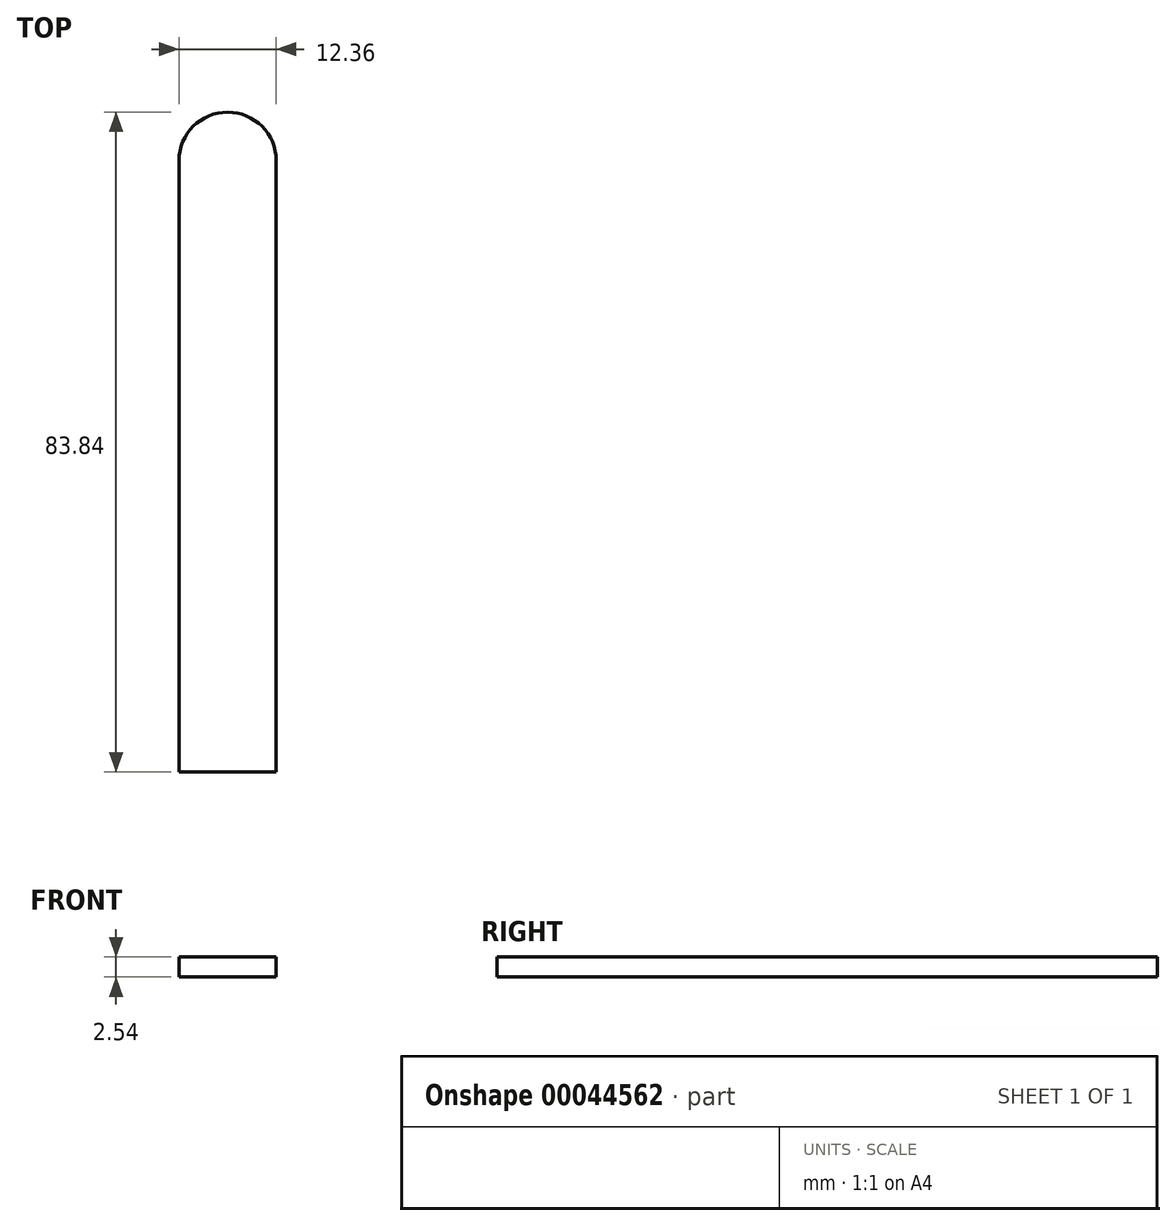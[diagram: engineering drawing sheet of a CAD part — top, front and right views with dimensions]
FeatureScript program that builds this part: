
annotation { "Feature Type Name" : "Feature", "Feature Type Description" : "" }
export const myFeature = defineFeature(function(context is Context, id is Id, definition is map)
    precondition{}
    {
        {
            var Q0;
            Q0=qCreatedBy(makeId("Top.planeOp"),FACE);
            var sketch = newSketch(context, id + "F0", { "sketchPlane" : qUnion([Q0])});
            skLineSegment(sketch, "E0.rect.bottom", {"start": v(6.18, 38.83) * mm, "end": v(-6.18, 38.83) * mm});
            skLineSegment(sketch, "E0.rect.top", {"start": v(6.18, -38.83) * mm, "end": v(-6.18, -38.83) * mm});
            skLineSegment(sketch, "E0.rect.left", {"start": v(6.18, 38.83) * mm, "end": v(6.18, -38.83) * mm});
            skLineSegment(sketch, "E0.rect.right", {"start": v(-6.18, 38.83) * mm, "end": v(-6.18, -38.83) * mm});
            skPoint(sketch, "E0.rect.middle", {"position": v(0, 0) * mm});
            skArc(sketch, "E1", {"start": v(-6.18, 38.83) * mm, "mid": v(0, 45) * mm, "end": v(6.18, 38.83) * mm});
            skSolve(sketch);
        }
        {
            var Q0;
            Q0 = qSketchRegion(id + "F0", true);
            extrude(context, id + "F1", {"entities" : qUnion([Q0]), "depth" : 2.54 * mm});
        }
    });
